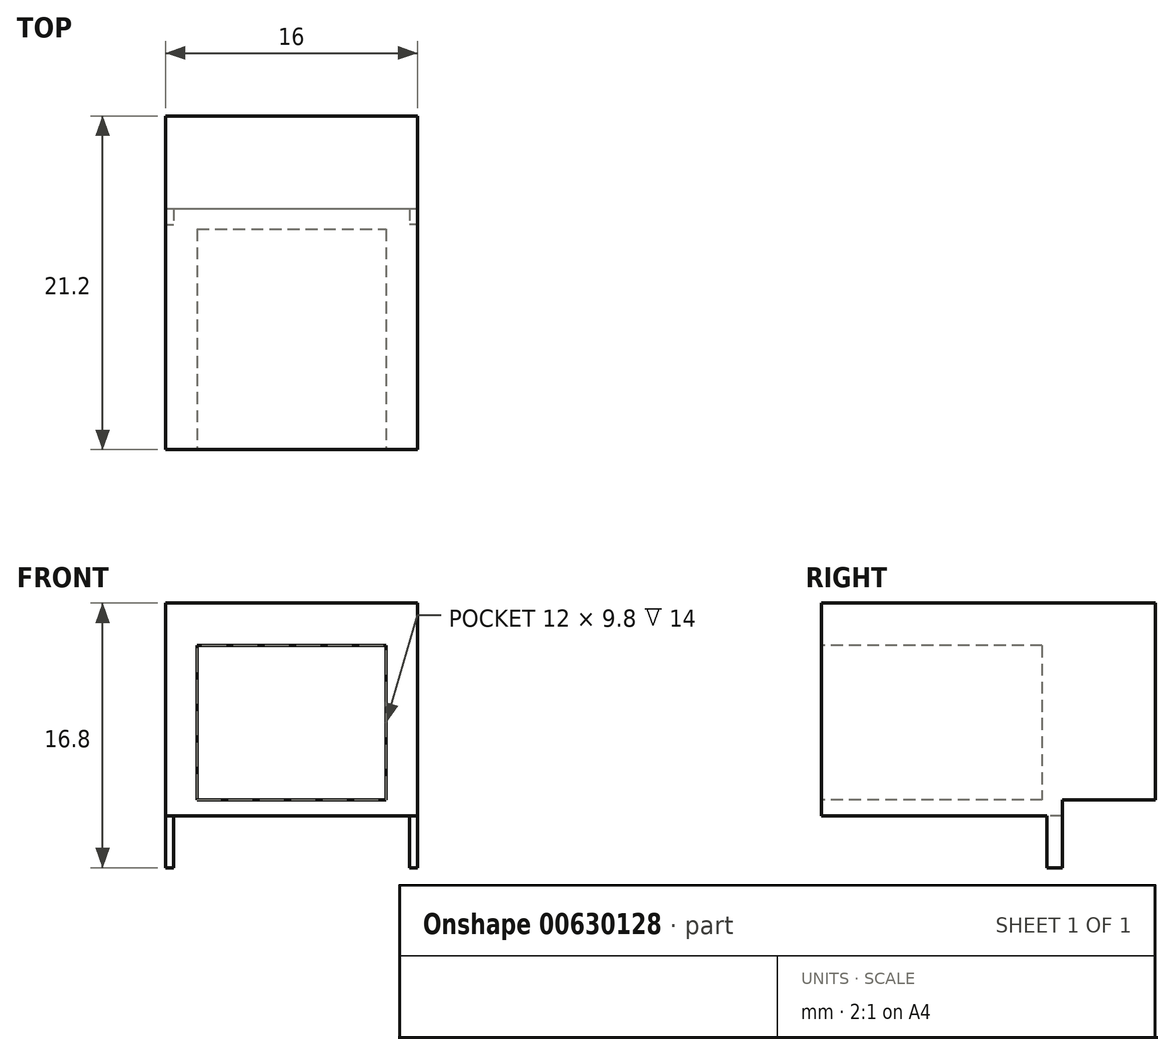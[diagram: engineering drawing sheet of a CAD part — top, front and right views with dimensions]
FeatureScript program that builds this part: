
annotation { "Feature Type Name" : "Feature", "Feature Type Description" : "" }
export const myFeature = defineFeature(function(context is Context, id is Id, definition is map)
    precondition{}
    {
        {
            var Q0;
            Q0=qCreatedBy(makeId("Top.planeOp"),FACE);
            var sketch = newSketch(context, id + "F0", { "sketchPlane" : qUnion([Q0])});
            skLineSegment(sketch, "E0.bottom", {"start": v(0, 0) * mm, "end": v(16, 0) * mm});
            skLineSegment(sketch, "E0.top", {"start": v(0, 21.2) * mm, "end": v(16, 21.2) * mm});
            skLineSegment(sketch, "E0.left", {"start": v(0, 0) * mm, "end": v(0, 21.2) * mm});
            skLineSegment(sketch, "E0.right", {"start": v(16, 0) * mm, "end": v(16, 21.2) * mm});
            skSolve(sketch);
        }
        {
            var Q0;
            Q0=qSketchRegion(id+"F0",true);
            extrude(context, id + "F1", {"entities" : qUnion([Q0]), "depth" : 13.5 * mm});
        }
        {
            var Q0;
            Q0=makeQuery(id+"F1.opExtrude","SWEPT_FACE",FACE,{"disambiguationData":[OSD([sQuery(id+"F0.wireOp",EDGE,"E0.right")])]});
            var sketch = newSketch(context, id + "F2", { "sketchPlane" : qUnion([Q0])});
            skLineSegment(sketch, "E1.bottom", {"start": v(21.2, 0) * mm, "end": v(15.3, 0) * mm});
            skLineSegment(sketch, "E1.top", {"start": v(21.2, 1) * mm, "end": v(15.3, 1) * mm});
            skLineSegment(sketch, "E1.left", {"start": v(21.2, 0) * mm, "end": v(21.2, 1) * mm});
            skLineSegment(sketch, "E1.right", {"start": v(15.3, 0) * mm, "end": v(15.3, 1) * mm});
            skSolve(sketch);
        }
        {
            var Q0;
            Q0=qSketchRegion(id+"F2",true);
            extrude(context, id + "F3", {"entities" : qUnion([Q0]), "operationType" : NewBodyOperationType.REMOVE, "endBound" : BoundingType.UP_TO_NEXT, "oppositeDirection" : true, "depth" : 25 * mm});
        }
        {
            var Q0;
            Q0=makeQuery(id+"F1.opExtrude","SWEPT_FACE",FACE,{"disambiguationData":[OSD([sQuery(id+"F0.wireOp",EDGE,"E0.bottom")])]});
            var sketch = newSketch(context, id + "F4", { "sketchPlane" : qUnion([Q0])});
            skLineSegment(sketch, "E2.bottom", {"start": v(2, 10.8) * mm, "end": v(14, 10.8) * mm});
            skLineSegment(sketch, "E2.top", {"start": v(2, 1) * mm, "end": v(14, 1) * mm});
            skLineSegment(sketch, "E2.left", {"start": v(2, 10.8) * mm, "end": v(2, 1) * mm});
            skLineSegment(sketch, "E2.right", {"start": v(14, 10.8) * mm, "end": v(14, 1) * mm});
            skSolve(sketch);
        }
        {
            var Q0;
            Q0=qSketchRegion(id+"F4",true);
            extrude(context, id + "F5", {"entities" : qUnion([Q0]), "operationType" : NewBodyOperationType.REMOVE, "oppositeDirection" : true, "depth" : 14 * mm});
        }
        {
            var Q0;
            Q0=makeQuery(id+"F1.opExtrude","CAP_FACE",FACE,{"disambiguationData":[OSD([sQuery(id+"F0.wireOp",EDGE,"E0.bottom"),sQuery(id+"F0.wireOp",EDGE,"E0.top"),sQuery(id+"F0.wireOp",EDGE,"E0.left"),sQuery(id+"F0.wireOp",EDGE,"E0.right")])],"isStart":true});
            var sketch = newSketch(context, id + "F6", { "sketchPlane" : qUnion([Q0])});
            skLineSegment(sketch, "E3.bottom", {"start": v(0, -15.3) * mm, "end": v(0.5, -15.3) * mm});
            skLineSegment(sketch, "E3.top", {"start": v(0, -14.3) * mm, "end": v(0.5, -14.3) * mm});
            skLineSegment(sketch, "E3.left", {"start": v(0, -15.3) * mm, "end": v(0, -14.3) * mm});
            skLineSegment(sketch, "E3.right", {"start": v(0.5, -15.3) * mm, "end": v(0.5, -14.3) * mm});
            skLineSegment(sketch, "E4.bottom", {"start": v(16, -15.3) * mm, "end": v(15.5, -15.3) * mm});
            skLineSegment(sketch, "E4.top", {"start": v(16, -14.3) * mm, "end": v(15.5, -14.3) * mm});
            skLineSegment(sketch, "E4.left", {"start": v(16, -15.3) * mm, "end": v(16, -14.3) * mm});
            skLineSegment(sketch, "E4.right", {"start": v(15.5, -15.3) * mm, "end": v(15.5, -14.3) * mm});
            skSolve(sketch);
        }
        {
            var Q0;
            Q0=qSketchRegion(id+"F6",true);
            extrude(context, id + "F7", {"entities" : qUnion([Q0]), "operationType" : NewBodyOperationType.ADD, "depth" : 3.3 * mm});
        }
    });
